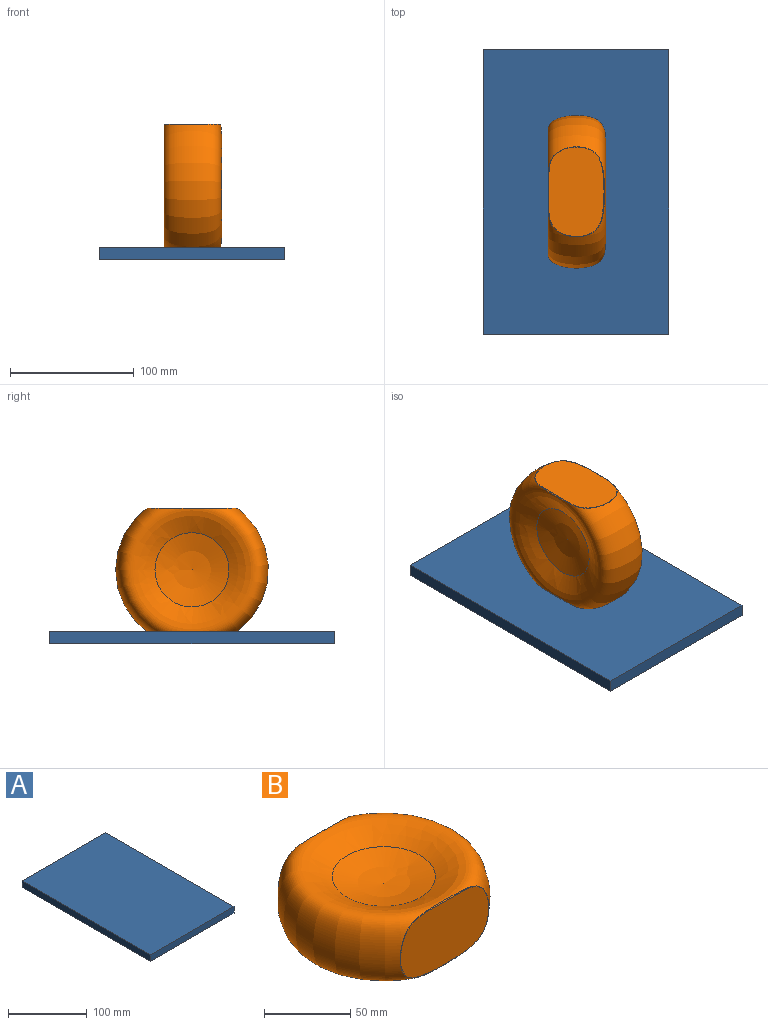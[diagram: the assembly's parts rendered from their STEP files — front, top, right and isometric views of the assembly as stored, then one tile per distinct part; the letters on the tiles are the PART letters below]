
ASSEMBLY  parts=2 mates=1
PART A: 6 faces, bbox 150x230x10 mm
  f0: plane 230x10mm, normal (-1,0,0), area 2300mm2, adj f1,f3,f4,f5
  f1: plane 150x10mm, normal (0,-1,0), area 1500mm2, adj f0,f2,f4,f5
  f2: plane 230x10mm, normal (1,0,0), area 2300mm2, adj f1,f3,f4,f5
  f3: plane 150x10mm, normal (0,1,0), area 1500mm2, adj f0,f2,f4,f5
  f4: plane 230x150mm, normal (0,0,1), area 34500mm2, adj f0,f1,f2,f3
  f5: plane 230x150mm, normal (0,0,-1), area 34500mm2, adj f0,f1,f2,f3
PART B: 7 faces, bbox 123.6x123.6x46.5 mm
  f0: revolved ~123.58x123.58mm, area 24023.9mm2, adj f1,f2,f5,f6
  f1: sphere r=90mm, area 2910.7mm2, adj f0
  f2: sphere r=300mm, area 2834.5mm2, adj f0
  f3: plane 72.48x44.94mm, normal (0,1,0), area 2818.5mm2, adj f5
  f4: plane 72.47x44.94mm, normal (0,-1,0), area 2818.1mm2, adj f6
  f5: bspline ~72.89x45.72mm, area 74.2mm2, adj f0,f3
  f6: bspline ~72.89x45.72mm, area 73mm2, adj f0,f4
PLACE A at identity fixed
PLACE B rot(axis=(-0.58,-0.58,0.58),120deg) t=(-212.61,30.6,60)mm
MATE fastened B.f3 <-> A.f4  axis (0,0,-1) through (-212.8,30.6,10)mm
